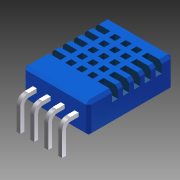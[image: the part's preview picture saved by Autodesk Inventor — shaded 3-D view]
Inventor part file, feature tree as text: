
AUTODESK INVENTOR PART (.ipt)
format: ipt  version: 2012 (Build 160160000, 160)  size: 378,368 bytes
history: native  units: mm
features: extrude x6, sketch x6, fillet x2, chamfer x1, pattern_linear x1
ambient origin geometry x8: Origin, YZ Plane, XZ Plane, XY Plane, X Axis, Y Axis, Z Axis, Center Point
bodies: Solid1 (feature_tree)
feature tree (16):
  extrude  "Extrusion1"  Depth=15.5mm
  extrude  "Extrusion2"  Depth=6.0mm
  chamfer  "Chamfer1"  Distance=5.5mm
  extrude  "Extrusion3"  Depth=1.1mm
  extrude  "Extrusion4"  Depth=50.0mm
  extrude  "Extrusion5"  Depth=1.1mm
  extrude  "Extrusion6"  Depth=0.875mm
  pattern_linear  "Rectangular Pattern2"  Spacing1=0.875mm  [1 undecoded]
  fillet  "Fillet3"  Radius=0.875mm
  fillet  "Fillet4"  Radius=50.0mm
  sketch  "Sketch1"  dims[d0=12.0mm d1=15.5mm]
  sketch  "Sketch2"  dims[d2=7.75mm d3=6.0mm d4=5.5mm d5=0.0mm]
  sketch  "Sketch3"  dims[d6=2.6mm d7=1.1mm]
  sketch  "Sketch4"  dims[d8=4.5mm d9=50.0mm d11=2.0mm d12=10.0mm d14=10.0mm]
  sketch  "Sketch5"  dims[d16=1.1mm d17=1.1mm]
  sketch  "Sketch6"  dims[d18=1.1mm d19=0.875mm d20=0.875mm d21=0.875mm d22=50.0mm d24=2.0mm d25=10.0mm d27=10.0mm d29=2.0mm d30=0.0mm d31=0.5mm d32=2.0mm d33=45.0deg d34=1.1mm d35=8.0mm d36=1.2mm d37=4.8mm d38=2.0mm d39=0.0mm d40=0.7mm d41=0.7mm d42=40.0mm d44=2.54mm d45=10.0mm d47=10.0mm d49=0.92mm d50=2.4mm d51=8.0mm d52=0.0mm d53=5.0mm d54=0.0mm d55=0.7mm d56=5.0mm d57=0.0mm d63=40.0mm d65=2.54mm d66=1.5mm d67=0.9mm]
note: 1 required parameter value undecoded (feature->parameter linkage not recoverable at this tier; creation-order binding heuristic only, values carry confidence <= 0.55)
